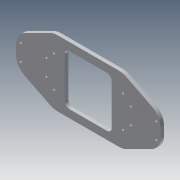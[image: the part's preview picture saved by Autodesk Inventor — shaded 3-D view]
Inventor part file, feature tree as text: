
AUTODESK INVENTOR PART (.ipt)
format: ipt  version: 2014 (Build 180170000, 170)  size: 157,184 bytes
history: native  units: mm
features: extrude x3, sketch x3, fillet x2
ambient origin geometry x8: Origin, YZ Plane, XZ Plane, XY Plane, X Axis, Y Axis, Z Axis, Center Point
bodies: Solid1 (feature_tree)
feature tree (8):
  extrude  "Extrusion1"  Depth=105.0mm
  extrude  "Extrusion2"  Depth=175.0mm
  fillet  "Fillet1"  Radius=87.5mm
  extrude  "Extrusion3"  Depth=8.0mm
  fillet  "Fillet2"  Radius=80.0mm
  sketch  "Sketch1"  dims[d0=105.0mm d3=26.0mm]
  sketch  "Sketch2"  dims[d4=41.0mm d5=175.0mm d6=87.5mm]
  sketch  "Sketch4"  dims[d7=230.0mm d8=4.0mm d9=80.0mm d10=75.0mm d11=5.588mm d12=0.0mm d13=60.0mm d14=30.0mm d15=10.0mm d16=0.0mm d17=25.0mm d18=4.0mm d20=50.0mm d21=10.0mm d22=0.0mm d23=110.0mm d24=8.0mm]
